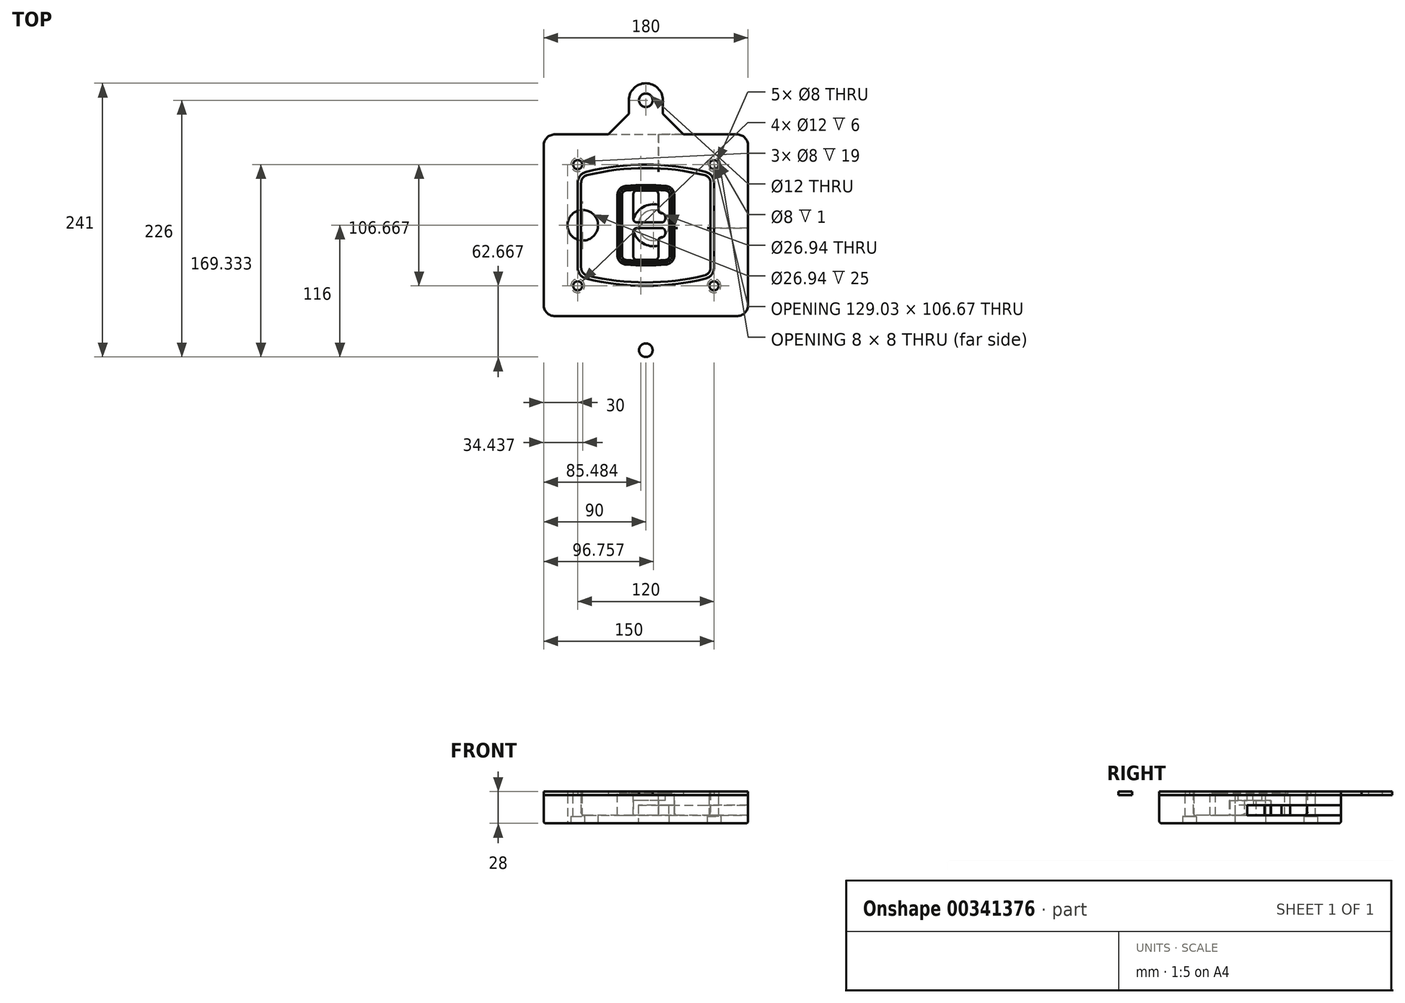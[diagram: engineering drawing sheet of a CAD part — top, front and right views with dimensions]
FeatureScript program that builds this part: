
annotation { "Feature Type Name" : "Feature", "Feature Type Description" : "" }
export const myFeature = defineFeature(function(context is Context, id is Id, definition is map)
    precondition{}
    {
        {
            var Q0;
            Q0=qCreatedBy(makeId("Top.planeOp"),FACE);
            var sketch = newSketch(context, id + "F0", { "sketchPlane" : qUnion([Q0])});
            skPoint(sketch, "E0.rect.middle", {"position": v(0, 0) * mm});
            skLineSegment(sketch, "E1.bottom", {"start": v(-80, -80) * mm, "end": v(80, -80) * mm});
            skLineSegment(sketch, "E1.top", {"start": v(-80, 80) * mm, "end": v(80, 80) * mm});
            skLineSegment(sketch, "E1.left", {"start": v(-90, -70) * mm, "end": v(-90, 70) * mm});
            skLineSegment(sketch, "E1.right", {"start": v(90, -70) * mm, "end": v(90, 70) * mm});
            skLineSegment(sketch, "E2", {"start": v(-90, 80) * mm, "end": v(90, -80) * mm, "construction": true});
            skLineSegment(sketch, "E3", {"start": v(90, 80) * mm, "end": v(-90, -80) * mm, "construction": true});
            skCircle(sketch, "E4", {"center": v(-60, 53.33) * mm, "radius": 4 * mm});
            skCircle(sketch, "E5", {"center": v(60, 53.33) * mm, "radius": 4 * mm});
            skCircle(sketch, "E6", {"center": v(60, -53.33) * mm, "radius": 4 * mm});
            skCircle(sketch, "E7", {"center": v(-60, -53.33) * mm, "radius": 4 * mm});
            skLineSegment(sketch, "E8", {"start": v(-60, 53.33) * mm, "end": v(60, 53.33) * mm, "construction": true});
            skLineSegment(sketch, "E9", {"start": v(60, 53.33) * mm, "end": v(60, -53.33) * mm, "construction": true});
            skLineSegment(sketch, "E10", {"start": v(60, -53.33) * mm, "end": v(-60, -53.33) * mm, "construction": true});
            skLineSegment(sketch, "E11", {"start": v(-60, -53.33) * mm, "end": v(-60, 53.33) * mm, "construction": true});
            skLineSegment(sketch, "E12", {"start": v(-60, 37.3) * mm, "end": v(-60, -37.3) * mm});
            skLineSegment(sketch, "E13", {"start": v(60, 37.3) * mm, "end": v(60, -37.3) * mm});
            skArc(sketch, "E14", {"start": v(52.38, 47.01) * mm, "mid": v(0, 53.33) * mm, "end": v(-52.38, 47.01) * mm});
            skArc(sketch, "E15", {"start": v(-52.38, -47.01) * mm, "mid": v(0, -53.33) * mm, "end": v(52.38, -47.01) * mm});
            skLineSegment(sketch, "E16", {"start": v(-60, 0) * mm, "end": v(60, 0) * mm, "construction": true});
            skPoint(sketch, "E17.visualSharp", {"position": v(-60, -45) * mm});
            skArc(sketch, "E17.filletArc", {"start": v(-60, -37.3) * mm, "mid": v(-57.87, -43.47) * mm, "end": v(-52.38, -47.01) * mm});
            skPoint(sketch, "E18.visualSharp", {"position": v(-60, 45) * mm});
            skArc(sketch, "E18.filletArc", {"start": v(-52.38, 47.01) * mm, "mid": v(-57.87, 43.47) * mm, "end": v(-60, 37.3) * mm});
            skPoint(sketch, "E19.visualSharp", {"position": v(60, 45) * mm});
            skArc(sketch, "E19.filletArc", {"start": v(60, 37.3) * mm, "mid": v(57.87, 43.47) * mm, "end": v(52.38, 47.01) * mm});
            skPoint(sketch, "E20.visualSharp", {"position": v(60, -45) * mm});
            skArc(sketch, "E20.filletArc", {"start": v(52.38, -47.01) * mm, "mid": v(57.87, -43.47) * mm, "end": v(60, -37.3) * mm});
            skPoint(sketch, "E21.visualSharp", {"position": v(-90, 80) * mm});
            skArc(sketch, "E21.filletArc", {"start": v(-80, 80) * mm, "mid": v(-87.07, 77.07) * mm, "end": v(-90, 70) * mm});
            skPoint(sketch, "E22.visualSharp", {"position": v(90, 80) * mm});
            skArc(sketch, "E22.filletArc", {"start": v(90, 70) * mm, "mid": v(87.07, 77.07) * mm, "end": v(80, 80) * mm});
            skPoint(sketch, "E23.visualSharp", {"position": v(90, -80) * mm});
            skArc(sketch, "E23.filletArc", {"start": v(80, -80) * mm, "mid": v(87.07, -77.07) * mm, "end": v(90, -70) * mm});
            skPoint(sketch, "E24.visualSharp", {"position": v(-90, -80) * mm});
            skArc(sketch, "E24.filletArc", {"start": v(-90, -70) * mm, "mid": v(-87.07, -77.07) * mm, "end": v(-80, -80) * mm});
            skArc(sketch, "E25.0", {"start": v(57, 37.3) * mm, "mid": v(55.5, 41.62) * mm, "end": v(51.67, 44.1) * mm});
            skLineSegment(sketch, "E25.1", {"start": v(57, 37.3) * mm, "end": v(57, -37.3) * mm});
            skArc(sketch, "E25.2", {"start": v(51.67, -44.1) * mm, "mid": v(55.5, -41.62) * mm, "end": v(57, -37.3) * mm});
            skArc(sketch, "E25.3", {"start": v(-51.67, -44.1) * mm, "mid": v(0, -50.33) * mm, "end": v(51.67, -44.1) * mm});
            skArc(sketch, "E25.4", {"start": v(-57, -37.3) * mm, "mid": v(-55.5, -41.62) * mm, "end": v(-51.67, -44.1) * mm});
            skArc(sketch, "E25.5", {"start": v(51.67, 44.1) * mm, "mid": v(0, 50.33) * mm, "end": v(-51.67, 44.1) * mm});
            skLineSegment(sketch, "E25.6", {"start": v(-57, 37.3) * mm, "end": v(-57, -37.3) * mm});
            skArc(sketch, "E25.7", {"start": v(-51.67, 44.1) * mm, "mid": v(-55.5, 41.62) * mm, "end": v(-57, 37.3) * mm});
            skArc(sketch, "E26.0", {"start": v(-53.33, 50.9) * mm, "mid": v(-61.01, 45.94) * mm, "end": v(-64, 37.3) * mm});
            skArc(sketch, "E26.1", {"start": v(53.33, 50.9) * mm, "mid": v(0, 57.33) * mm, "end": v(-53.33, 50.9) * mm});
            skArc(sketch, "E26.2", {"start": v(64, 37.3) * mm, "mid": v(61.01, 45.94) * mm, "end": v(53.33, 50.9) * mm});
            skLineSegment(sketch, "E26.3", {"start": v(64, 37.3) * mm, "end": v(64, -37.3) * mm});
            skArc(sketch, "E26.4", {"start": v(53.33, -50.9) * mm, "mid": v(61.01, -45.94) * mm, "end": v(64, -37.3) * mm});
            skLineSegment(sketch, "E26.5", {"start": v(-64, 37.3) * mm, "end": v(-64, -37.3) * mm});
            skArc(sketch, "E26.6", {"start": v(-53.33, -50.9) * mm, "mid": v(0, -57.33) * mm, "end": v(53.33, -50.9) * mm});
            skArc(sketch, "E26.7", {"start": v(-64, -37.3) * mm, "mid": v(-61.01, -45.94) * mm, "end": v(-53.33, -50.9) * mm});
            skSolve(sketch);
        }
        {
            var Q0;
            Q0=makeQuery(id+"F0.imprint","IMPRINT",FACE,{"disambiguationData":[TD([[makeQuery(id+"F0.imprint","IMPRINT",EDGE,{"derivedFrom":sQuery(id+"F0.wireOp",EDGE,"E1.bottom")}),1.0]])]});
            var Q1;
            Q1=makeQuery(id+"F0.imprint","IMPRINT",FACE,{"disambiguationData":[TD([[makeQuery(id+"F0.imprint","IMPRINT",EDGE,{"derivedFrom":sQuery(id+"F0.wireOp",EDGE,"E12")}),1.0]])]});
            var Q2;
            Q2=makeQuery(id+"F0.imprint","IMPRINT",FACE,{"disambiguationData":[TD([[makeQuery(id+"F0.imprint","IMPRINT",EDGE,{"derivedFrom":sQuery(id+"F0.wireOp",EDGE,"E25.0")}),1.0]])]});
            var Q3;
            Q3=makeQuery(id+"F0.imprint","IMPRINT",FACE,{"disambiguationData":[TD([[makeQuery(id+"F0.imprint","IMPRINT",EDGE,{"derivedFrom":sQuery(id+"F0.wireOp",EDGE,"E12")}),-1.0]])]});
            extrude(context, id + "F1", {"entities" : qUnion([Q0, Q1, Q2, Q3]), "oppositeDirection" : true, "depth" : 25 * mm});
        }
        {
            var Q0;
            Q0=makeQuery(id+"F0.imprint","IMPRINT",FACE,{"disambiguationData":[TD([[makeQuery(id+"F0.imprint","IMPRINT",EDGE,{"derivedFrom":sQuery(id+"F0.wireOp",EDGE,"E12")}),1.0]])]});
            extrude(context, id + "F2", {"entities" : qUnion([Q0]), "operationType" : NewBodyOperationType.ADD, "depth" : 3 * mm});
        }
        {
            var Q0;
            Q0=makeQuery(id+"F0.imprint","IMPRINT",FACE,{"disambiguationData":[TD([[makeQuery(id+"F0.imprint","IMPRINT",EDGE,{"derivedFrom":sQuery(id+"F0.wireOp",EDGE,"E25.0")}),1.0]])]});
            extrude(context, id + "F3", {"entities" : qUnion([Q0]), "operationType" : NewBodyOperationType.REMOVE, "oppositeDirection" : true, "depth" : 18 * mm});
        }
        {
            var Q0;
            Q0=makeQuery(id+"F2.opExtrude","CAP_FACE",FACE,{"disambiguationData":[OSD([sQuery(id+"F0.wireOp",EDGE,"E12"),sQuery(id+"F0.wireOp",EDGE,"E13"),sQuery(id+"F0.wireOp",EDGE,"E14"),sQuery(id+"F0.wireOp",EDGE,"E15"),sQuery(id+"F0.wireOp",EDGE,"E17.filletArc"),sQuery(id+"F0.wireOp",EDGE,"E18.filletArc"),sQuery(id+"F0.wireOp",EDGE,"E19.filletArc"),sQuery(id+"F0.wireOp",EDGE,"E20.filletArc"),sQuery(id+"F0.wireOp",EDGE,"E25.0"),sQuery(id+"F0.wireOp",EDGE,"E25.1"),sQuery(id+"F0.wireOp",EDGE,"E25.2"),sQuery(id+"F0.wireOp",EDGE,"E25.3"),sQuery(id+"F0.wireOp",EDGE,"E25.4"),sQuery(id+"F0.wireOp",EDGE,"E25.5"),sQuery(id+"F0.wireOp",EDGE,"E25.6"),sQuery(id+"F0.wireOp",EDGE,"E25.7")])],"isStart":false});
            var sketch = newSketch(context, id + "F4", { "sketchPlane" : qUnion([Q0])});
            skArc(sketch, "E27.0", {"start": v(-17.7, -34.56) * mm, "mid": v(0, -35.33) * mm, "end": v(17.7, -34.56) * mm});
            skArc(sketch, "E28.0", {"start": v(17.7, 34.56) * mm, "mid": v(0, 35.33) * mm, "end": v(-17.7, 34.56) * mm});
            skLineSegment(sketch, "E29", {"start": v(-25, 26.59) * mm, "end": v(-25, -26.59) * mm});
            skLineSegment(sketch, "E30", {"start": v(25, 26.59) * mm, "end": v(25, -26.59) * mm});
            skLineSegment(sketch, "E31", {"start": v(-25, 33.78) * mm, "end": v(25, 33.78) * mm, "construction": true});
            skLineSegment(sketch, "E32", {"start": v(-25, -33.78) * mm, "end": v(25, -33.78) * mm, "construction": true});
            skPoint(sketch, "E33.visualSharp", {"position": v(-25, 33.78) * mm});
            skArc(sketch, "E33.filletArc", {"start": v(-17.7, 34.56) * mm, "mid": v(-22.9, 32) * mm, "end": v(-25, 26.59) * mm});
            skPoint(sketch, "E34.visualSharp", {"position": v(25, 33.78) * mm});
            skArc(sketch, "E34.filletArc", {"start": v(25, 26.59) * mm, "mid": v(22.9, 32) * mm, "end": v(17.7, 34.56) * mm});
            skPoint(sketch, "E35.visualSharp", {"position": v(25, -33.78) * mm});
            skArc(sketch, "E35.filletArc", {"start": v(17.7, -34.56) * mm, "mid": v(22.9, -32) * mm, "end": v(25, -26.59) * mm});
            skPoint(sketch, "E36.visualSharp", {"position": v(-25, -33.78) * mm});
            skArc(sketch, "E36.filletArc", {"start": v(-25, -26.59) * mm, "mid": v(-22.9, -32) * mm, "end": v(-17.7, -34.56) * mm});
            skArc(sketch, "E37.0", {"start": v(51.67, 44.1) * mm, "mid": v(0, 50.33) * mm, "end": v(-51.67, 44.1) * mm});
            skArc(sketch, "E37.1", {"start": v(-51.67, 44.1) * mm, "mid": v(-55.5, 41.62) * mm, "end": v(-57, 37.3) * mm});
            skLineSegment(sketch, "E37.2", {"start": v(-57, 37.3) * mm, "end": v(-57, -37.3) * mm});
            skArc(sketch, "E37.3", {"start": v(-57, -37.3) * mm, "mid": v(-55.5, -41.62) * mm, "end": v(-51.67, -44.1) * mm});
            skArc(sketch, "E37.4", {"start": v(-51.67, -44.1) * mm, "mid": v(0, -50.33) * mm, "end": v(51.67, -44.1) * mm});
            skArc(sketch, "E37.5", {"start": v(51.67, -44.1) * mm, "mid": v(55.5, -41.62) * mm, "end": v(57, -37.3) * mm});
            skLineSegment(sketch, "E37.6", {"start": v(57, 37.3) * mm, "end": v(57, -37.3) * mm});
            skArc(sketch, "E37.7", {"start": v(57, 37.3) * mm, "mid": v(55.5, 41.62) * mm, "end": v(51.67, 44.1) * mm});
            skLineSegment(sketch, "E38.0", {"start": v(23, 26.59) * mm, "end": v(23, -26.59) * mm});
            skArc(sketch, "E38.1", {"start": v(17.53, -32.56) * mm, "mid": v(21.42, -30.64) * mm, "end": v(23, -26.59) * mm});
            skArc(sketch, "E38.2", {"start": v(-17.53, -32.56) * mm, "mid": v(0, -33.33) * mm, "end": v(17.53, -32.56) * mm});
            skArc(sketch, "E38.3", {"start": v(-23, -26.59) * mm, "mid": v(-21.42, -30.64) * mm, "end": v(-17.53, -32.56) * mm});
            skLineSegment(sketch, "E38.4", {"start": v(-23, 26.59) * mm, "end": v(-23, -26.59) * mm});
            skArc(sketch, "E38.5", {"start": v(23, 26.59) * mm, "mid": v(21.42, 30.64) * mm, "end": v(17.53, 32.56) * mm});
            skArc(sketch, "E38.6", {"start": v(-17.53, 32.56) * mm, "mid": v(-21.42, 30.64) * mm, "end": v(-23, 26.59) * mm});
            skArc(sketch, "E38.7", {"start": v(17.53, 32.56) * mm, "mid": v(0, 33.33) * mm, "end": v(-17.53, 32.56) * mm});
            skArc(sketch, "E39.0", {"start": v(21, 26.59) * mm, "mid": v(19.95, 29.29) * mm, "end": v(17.35, 30.57) * mm});
            skLineSegment(sketch, "E39.1", {"start": v(21, 26.59) * mm, "end": v(21, -26.59) * mm});
            skArc(sketch, "E39.2", {"start": v(17.35, -30.57) * mm, "mid": v(19.95, -29.29) * mm, "end": v(21, -26.59) * mm});
            skArc(sketch, "E39.3", {"start": v(-17.35, -30.57) * mm, "mid": v(0, -31.33) * mm, "end": v(17.35, -30.57) * mm});
            skArc(sketch, "E39.4", {"start": v(-21, -26.59) * mm, "mid": v(-19.95, -29.29) * mm, "end": v(-17.35, -30.57) * mm});
            skArc(sketch, "E39.5", {"start": v(17.35, 30.57) * mm, "mid": v(0, 31.33) * mm, "end": v(-17.35, 30.57) * mm});
            skLineSegment(sketch, "E39.6", {"start": v(-21, 26.59) * mm, "end": v(-21, -26.59) * mm});
            skArc(sketch, "E39.7", {"start": v(-17.35, 30.57) * mm, "mid": v(-19.95, 29.29) * mm, "end": v(-21, 26.59) * mm});
            skLineSegment(sketch, "E40", {"start": v(-25, 0) * mm, "end": v(25, 0) * mm, "construction": true});
            skLineSegment(sketch, "E41", {"start": v(-11, 5.5) * mm, "end": v(-11, 27.5) * mm});
            skLineSegment(sketch, "E42", {"start": v(-8, 30.5) * mm, "end": v(8, 30.5) * mm});
            skLineSegment(sketch, "E43", {"start": v(11, 27.5) * mm, "end": v(11, 13.5) * mm});
            skLineSegment(sketch, "E44", {"start": v(14, 10.5) * mm, "end": v(14, 10.5) * mm});
            skLineSegment(sketch, "E45", {"start": v(17, 7.5) * mm, "end": v(17, 5.5) * mm});
            skLineSegment(sketch, "E46", {"start": v(14, 2.5) * mm, "end": v(-8, 2.5) * mm});
            skPoint(sketch, "E47.visualSharp", {"position": v(-11, 30.5) * mm});
            skArc(sketch, "E47.filletArc", {"start": v(-8, 30.5) * mm, "mid": v(-10.12, 29.62) * mm, "end": v(-11, 27.5) * mm});
            skPoint(sketch, "E48.visualSharp", {"position": v(11, 30.5) * mm});
            skArc(sketch, "E48.filletArc", {"start": v(11, 27.5) * mm, "mid": v(10.12, 29.62) * mm, "end": v(8, 30.5) * mm});
            skPoint(sketch, "E49.visualSharp", {"position": v(11, 10.5) * mm});
            skArc(sketch, "E49.filletArc", {"start": v(11, 13.5) * mm, "mid": v(11.88, 11.38) * mm, "end": v(14, 10.5) * mm});
            skPoint(sketch, "E50.visualSharp", {"position": v(17, 10.5) * mm});
            skArc(sketch, "E50.filletArc", {"start": v(17, 7.5) * mm, "mid": v(16.12, 9.62) * mm, "end": v(14, 10.5) * mm});
            skPoint(sketch, "E51.visualSharp", {"position": v(17, 2.5) * mm});
            skArc(sketch, "E51.filletArc", {"start": v(14, 2.5) * mm, "mid": v(16.12, 3.38) * mm, "end": v(17, 5.5) * mm});
            skPoint(sketch, "E52.visualSharp", {"position": v(-11, 2.5) * mm});
            skArc(sketch, "E52.filletArc", {"start": v(-11, 5.5) * mm, "mid": v(-10.12, 3.38) * mm, "end": v(-8, 2.5) * mm});
            skLineSegment(sketch, "E53.0.MirrorCS", {"start": v(14, -2.5) * mm, "end": v(-8, -2.5) * mm});
            skArc(sketch, "E54.0.MirrorCS", {"start": v(-11, -5.5) * mm, "mid": v(-10.12, -3.38) * mm, "end": v(-8, -2.5) * mm});
            skLineSegment(sketch, "E55.0.MirrorCS", {"start": v(-11, -5.5) * mm, "end": v(-11, -27.5) * mm});
            skArc(sketch, "E56.0.MirrorCS", {"start": v(-8, -30.5) * mm, "mid": v(-10.12, -29.62) * mm, "end": v(-11, -27.5) * mm});
            skLineSegment(sketch, "E57.0.MirrorCS", {"start": v(-8, -30.5) * mm, "end": v(8, -30.5) * mm});
            skArc(sketch, "E58.0.MirrorCS", {"start": v(11, -27.5) * mm, "mid": v(10.12, -29.62) * mm, "end": v(8, -30.5) * mm});
            skLineSegment(sketch, "E59.0.MirrorCS", {"start": v(11, -27.5) * mm, "end": v(11, -13.5) * mm});
            skArc(sketch, "E60.0.MirrorCS", {"start": v(11, -13.5) * mm, "mid": v(11.88, -11.38) * mm, "end": v(14, -10.5) * mm});
            skArc(sketch, "E61.0.MirrorCS", {"start": v(17, -7.5) * mm, "mid": v(16.12, -9.62) * mm, "end": v(14, -10.5) * mm});
            skLineSegment(sketch, "E62.0.MirrorCS", {"start": v(17, -7.5) * mm, "end": v(17, -5.5) * mm});
            skArc(sketch, "E63.0.MirrorCS", {"start": v(14, -2.5) * mm, "mid": v(16.12, -3.38) * mm, "end": v(17, -5.5) * mm});
            skSolve(sketch);
        }
        {
            var Q0;
            Q0=makeQuery(id+"F4.imprint","IMPRINT",FACE,{"disambiguationData":[TD([[makeQuery(id+"F4.imprint","IMPRINT",EDGE,{"derivedFrom":sQuery(id+"F4.wireOp",EDGE,"E27.0")}),1.0]])]});
            var Q1;
            Q1=makeQuery(id+"F4.imprint","IMPRINT",FACE,{"disambiguationData":[TD([[makeQuery(id+"F4.imprint","IMPRINT",EDGE,{"derivedFrom":sQuery(id+"F4.wireOp",EDGE,"E38.0")}),-1.0]])]});
            var Q2;
            Q2=makeQuery(id+"F4.imprint","IMPRINT",FACE,{"disambiguationData":[TD([[makeQuery(id+"F4.imprint","IMPRINT",EDGE,{"derivedFrom":sQuery(id+"F4.wireOp",EDGE,"E39.0")}),1.0]])]});
            extrude(context, id + "F5", {"entities" : qUnion([Q0, Q1, Q2]), "operationType" : NewBodyOperationType.ADD, "endBound" : BoundingType.UP_TO_NEXT, "oppositeDirection" : true, "depth" : 25 * mm});
        }
        {
            var Q0;
            Q0=makeQuery(id+"F4.imprint","IMPRINT",FACE,{"disambiguationData":[TD([[makeQuery(id+"F4.imprint","IMPRINT",EDGE,{"derivedFrom":sQuery(id+"F4.wireOp",EDGE,"E38.0")}),-1.0]])]});
            extrude(context, id + "F6", {"entities" : qUnion([Q0]), "operationType" : NewBodyOperationType.REMOVE, "oppositeDirection" : true, "depth" : 2 * mm});
        }
        {
            var Q0;
            Q0=makeQuery(id+"F1.opExtrude","CAP_FACE",FACE,{"disambiguationData":[OSD([sQuery(id+"F0.wireOp",EDGE,"E1.bottom"),sQuery(id+"F0.wireOp",EDGE,"E1.top"),sQuery(id+"F0.wireOp",EDGE,"E1.left"),sQuery(id+"F0.wireOp",EDGE,"E1.right"),sQuery(id+"F0.wireOp",EDGE,"E4"),sQuery(id+"F0.wireOp",EDGE,"E5"),sQuery(id+"F0.wireOp",EDGE,"E6"),sQuery(id+"F0.wireOp",EDGE,"E7"),sQuery(id+"F0.wireOp",EDGE,"E21.filletArc"),sQuery(id+"F0.wireOp",EDGE,"E22.filletArc"),sQuery(id+"F0.wireOp",EDGE,"E23.filletArc"),sQuery(id+"F0.wireOp",EDGE,"E24.filletArc")])],"isStart":false});
            var sketch = newSketch(context, id + "F7", { "sketchPlane" : qUnion([Q0])});
            skCircle(sketch, "E64", {"center": v(6.76, 0) * mm, "radius": 13.47 * mm});
            skCircle(sketch, "E65", {"center": v(-55.56, 0) * mm, "radius": 13.47 * mm});
            skLineSegment(sketch, "E66", {"start": v(90, 0) * mm, "end": v(-90, 0) * mm});
            skCircle(sketch, "E67", {"center": v(6.76, 0) * mm, "radius": 18.47 * mm});
            skCircle(sketch, "E68", {"center": v(60, -53.33) * mm, "radius": 6 * mm});
            skCircle(sketch, "E69", {"center": v(-60, -53.33) * mm, "radius": 6 * mm});
            skCircle(sketch, "E70", {"center": v(-60, 53.33) * mm, "radius": 6 * mm});
            skCircle(sketch, "E71", {"center": v(60, 53.33) * mm, "radius": 6 * mm});
            skSolve(sketch);
        }
        {
            var Q0;
            {var subQ1=sQuery(id+"F7.wireOp",EDGE,"E66");var subQ4=sQuery(id+"F7.wireOp",EDGE,"E64");var subQ6=makeQuery(id+"F7.imprint","INTERSECT",VERTEX,{"disambiguationData":[OD(0.0)],"derivedFrom":[subQ4,subQ1]});Q0=makeQuery(id+"F7.imprint","IMPRINT",FACE,{"disambiguationData":[TD([[makeQuery(id+"F7.imprint","IMPRINT",EDGE,{"disambiguationData":[TD([[subQ6,-1.0]])],"derivedFrom":subQ4}),-1.0]])]});}
            var Q1;
            {var subQ0=sQuery(id+"F7.wireOp",EDGE,"E66");var subQ1=sQuery(id+"F7.wireOp",EDGE,"E64");var subQ3=makeQuery(id+"F7.imprint","INTERSECT",VERTEX,{"disambiguationData":[OD(0.0)],"derivedFrom":[subQ1,subQ0]});Q1=makeQuery(id+"F7.imprint","IMPRINT",FACE,{"disambiguationData":[TD([[makeQuery(id+"F7.imprint","IMPRINT",EDGE,{"disambiguationData":[TD([[subQ3,-1.0]])],"derivedFrom":subQ1}),1.0]])]});}
            var Q2;
            {var subQ0=sQuery(id+"F7.wireOp",EDGE,"E66");var subQ1=sQuery(id+"F7.wireOp",EDGE,"E64");var subQ3=makeQuery(id+"F7.imprint","INTERSECT",VERTEX,{"disambiguationData":[OD(0.0)],"derivedFrom":[subQ1,subQ0]});Q2=makeQuery(id+"F7.imprint","IMPRINT",FACE,{"disambiguationData":[TD([[makeQuery(id+"F7.imprint","IMPRINT",EDGE,{"disambiguationData":[TD([[subQ3,1.0]])],"derivedFrom":subQ1}),1.0]])]});}
            var Q3;
            {var subQ1=sQuery(id+"F7.wireOp",EDGE,"E66");var subQ4=sQuery(id+"F7.wireOp",EDGE,"E64");var subQ6=makeQuery(id+"F7.imprint","INTERSECT",VERTEX,{"disambiguationData":[OD(0.0)],"derivedFrom":[subQ4,subQ1]});Q3=makeQuery(id+"F7.imprint","IMPRINT",FACE,{"disambiguationData":[TD([[makeQuery(id+"F7.imprint","IMPRINT",EDGE,{"disambiguationData":[TD([[subQ6,1.0]])],"derivedFrom":subQ4}),-1.0]])]});}
            extrude(context, id + "F8", {"entities" : qUnion([Q0, Q1, Q2, Q3]), "operationType" : NewBodyOperationType.ADD, "oppositeDirection" : true, "depth" : 20 * mm});
        }
        {
            var Q0;
            {var subQ0=sQuery(id+"F7.wireOp",EDGE,"E66");var subQ1=sQuery(id+"F7.wireOp",EDGE,"E64");var subQ3=makeQuery(id+"F7.imprint","INTERSECT",VERTEX,{"disambiguationData":[OD(0.0)],"derivedFrom":[subQ1,subQ0]});Q0=makeQuery(id+"F7.imprint","IMPRINT",FACE,{"disambiguationData":[TD([[makeQuery(id+"F7.imprint","IMPRINT",EDGE,{"disambiguationData":[TD([[subQ3,-1.0]])],"derivedFrom":subQ1}),1.0]])]});}
            var Q1;
            {var subQ0=sQuery(id+"F7.wireOp",EDGE,"E66");var subQ1=sQuery(id+"F7.wireOp",EDGE,"E64");var subQ3=makeQuery(id+"F7.imprint","INTERSECT",VERTEX,{"disambiguationData":[OD(0.0)],"derivedFrom":[subQ1,subQ0]});Q1=makeQuery(id+"F7.imprint","IMPRINT",FACE,{"disambiguationData":[TD([[makeQuery(id+"F7.imprint","IMPRINT",EDGE,{"disambiguationData":[TD([[subQ3,1.0]])],"derivedFrom":subQ1}),1.0]])]});}
            extrude(context, id + "F9", {"entities" : qUnion([Q0, Q1]), "operationType" : NewBodyOperationType.REMOVE, "oppositeDirection" : true, "depth" : 16 * mm});
        }
        {
            var Q0;
            {var subQ0=sQuery(id+"F7.wireOp",EDGE,"E66");var subQ1=sQuery(id+"F7.wireOp",EDGE,"E65");var subQ3=makeQuery(id+"F7.imprint","INTERSECT",VERTEX,{"disambiguationData":[OD(0.0)],"derivedFrom":[subQ1,subQ0]});Q0=makeQuery(id+"F7.imprint","IMPRINT",FACE,{"disambiguationData":[TD([[makeQuery(id+"F7.imprint","IMPRINT",EDGE,{"disambiguationData":[TD([[subQ3,-1.0]])],"derivedFrom":subQ1}),1.0]])]});}
            var Q1;
            {var subQ0=sQuery(id+"F7.wireOp",EDGE,"E66");var subQ1=sQuery(id+"F7.wireOp",EDGE,"E65");var subQ3=makeQuery(id+"F7.imprint","INTERSECT",VERTEX,{"disambiguationData":[OD(0.0)],"derivedFrom":[subQ1,subQ0]});Q1=makeQuery(id+"F7.imprint","IMPRINT",FACE,{"disambiguationData":[TD([[makeQuery(id+"F7.imprint","IMPRINT",EDGE,{"disambiguationData":[TD([[subQ3,1.0]])],"derivedFrom":subQ1}),1.0]])]});}
            extrude(context, id + "F10", {"entities" : qUnion([Q0, Q1]), "operationType" : NewBodyOperationType.REMOVE, "oppositeDirection" : true, "depth" : 25 * mm});
        }
        {
            var Q0;
            Q0=makeQuery(id+"F7.imprint","IMPRINT",FACE,{"disambiguationData":[TD([[makeQuery(id+"F7.imprint","IMPRINT",EDGE,{"derivedFrom":sQuery(id+"F7.wireOp",EDGE,"E68")}),1.0]])]});
            var Q1;
            Q1=makeQuery(id+"F7.imprint","IMPRINT",FACE,{"disambiguationData":[TD([[makeQuery(id+"F7.imprint","IMPRINT",EDGE,{"derivedFrom":makeQuery(id+"F1.opExtrude","CAP_EDGE",EDGE,{"disambiguationData":[OSD([sQuery(id+"F0.wireOp",EDGE,"E5")])],"isStart":false})}),-1.0]])]});
            var Q2;
            Q2=makeQuery(id+"F7.imprint","IMPRINT",FACE,{"disambiguationData":[TD([[makeQuery(id+"F7.imprint","IMPRINT",EDGE,{"derivedFrom":sQuery(id+"F7.wireOp",EDGE,"E69")}),1.0]])]});
            var Q3;
            Q3=makeQuery(id+"F7.imprint","IMPRINT",FACE,{"disambiguationData":[TD([[makeQuery(id+"F7.imprint","IMPRINT",EDGE,{"derivedFrom":makeQuery(id+"F1.opExtrude","CAP_EDGE",EDGE,{"disambiguationData":[OSD([sQuery(id+"F0.wireOp",EDGE,"E4")])],"isStart":false})}),-1.0]])]});
            var Q4;
            Q4=makeQuery(id+"F7.imprint","IMPRINT",FACE,{"disambiguationData":[TD([[makeQuery(id+"F7.imprint","IMPRINT",EDGE,{"derivedFrom":sQuery(id+"F7.wireOp",EDGE,"E70")}),1.0]])]});
            var Q5;
            Q5=makeQuery(id+"F7.imprint","IMPRINT",FACE,{"disambiguationData":[TD([[makeQuery(id+"F7.imprint","IMPRINT",EDGE,{"derivedFrom":makeQuery(id+"F1.opExtrude","CAP_EDGE",EDGE,{"disambiguationData":[OSD([sQuery(id+"F0.wireOp",EDGE,"E7")])],"isStart":false})}),-1.0]])]});
            var Q6;
            Q6=makeQuery(id+"F7.imprint","IMPRINT",FACE,{"disambiguationData":[TD([[makeQuery(id+"F7.imprint","IMPRINT",EDGE,{"derivedFrom":sQuery(id+"F7.wireOp",EDGE,"E71")}),1.0]])]});
            var Q7;
            Q7=makeQuery(id+"F7.imprint","IMPRINT",FACE,{"disambiguationData":[TD([[makeQuery(id+"F7.imprint","IMPRINT",EDGE,{"derivedFrom":makeQuery(id+"F1.opExtrude","CAP_EDGE",EDGE,{"disambiguationData":[OSD([sQuery(id+"F0.wireOp",EDGE,"E6")])],"isStart":false})}),-1.0]])]});
            extrude(context, id + "F11", {"entities" : qUnion([Q0, Q1, Q2, Q3, Q4, Q5, Q6, Q7]), "operationType" : NewBodyOperationType.REMOVE, "oppositeDirection" : true, "depth" : 6 * mm});
        }
        {
            var Q0;
            Q0=makeQuery(id+"F9.boolean.opBoolean","COPY",FACE,{"derivedFrom":makeQuery(id+"F9.opExtrude","CAP_FACE",FACE,{"disambiguationData":[OSD([sQuery(id+"F7.wireOp",EDGE,"E64")])],"isStart":false})});
            var sketch = newSketch(context, id + "F12", { "sketchPlane" : qUnion([Q0])});
            skArc(sketch, "E72.0", {"start": v(11, -88.19) * mm, "mid": v(97.1, -83.6) * mm, "end": v(92.5, 2.5) * mm});
            skLineSegment(sketch, "E72.1", {"start": v(11, -17.97) * mm, "end": v(11, -17.97) * mm});
            skLineSegment(sketch, "E73", {"start": v(92.5, -105.13) * mm, "end": v(102.3, -105.13) * mm});
            skLineSegment(sketch, "E74.0", {"start": v(92.5, 2.5) * mm, "end": v(14, 2.5) * mm});
            skArc(sketch, "E74.1", {"start": v(14, 2.5) * mm, "mid": v(16.12, 3.38) * mm, "end": v(17, 5.5) * mm});
            skLineSegment(sketch, "E74.2", {"start": v(17, 7.5) * mm, "end": v(17, 5.5) * mm});
            skArc(sketch, "E74.3", {"start": v(17, 7.5) * mm, "mid": v(16.12, 9.62) * mm, "end": v(14, 10.5) * mm});
            skArc(sketch, "E74.4", {"start": v(11, 13.5) * mm, "mid": v(11.88, 11.38) * mm, "end": v(14, 10.5) * mm});
            skLineSegment(sketch, "E74.5", {"start": v(11, 13.5) * mm, "end": v(11, -88.19) * mm});
            skLineSegment(sketch, "E74.7", {"start": v(92.5, -2.5) * mm, "end": v(14, -2.5) * mm});
            skArc(sketch, "E74.8", {"start": v(14, -2.5) * mm, "mid": v(16.12, -3.38) * mm, "end": v(17, -5.5) * mm});
            skLineSegment(sketch, "E74.9", {"start": v(17, -7.5) * mm, "end": v(17, -5.5) * mm});
            skArc(sketch, "E74.10", {"start": v(17, -7.5) * mm, "mid": v(16.12, -9.62) * mm, "end": v(14, -10.5) * mm});
            skArc(sketch, "E74.11", {"start": v(11, -13.5) * mm, "mid": v(11.88, -11.38) * mm, "end": v(14, -10.5) * mm});
            skLineSegment(sketch, "E74.12", {"start": v(11, -17.97) * mm, "end": v(11, -13.5) * mm});
            skPoint(sketch, "E75.orphan", {"position": v(11, -27.5) * mm});
            skPoint(sketch, "E76.orphan", {"position": v(-8, -2.5) * mm});
            skPoint(sketch, "E77.orphan", {"position": v(-8, 2.5) * mm});
            skPoint(sketch, "E78.orphan", {"position": v(11, 27.5) * mm});
            skSolve(sketch);
        }
        {
            var Q0;
            {var subQ7=sQuery(id+"F12.wireOp",EDGE,"E72.0");var subQ14=sQuery(id+"F12.wireOp",EDGE,"E72.1");var subQ16=sQuery(id+"F12.wireOp",EDGE,"E74.1");var subQ18=sQuery(id+"F12.wireOp",EDGE,"E74.8");Q0=qUnion([makeQuery(id+"F12.imprint","IMPRINT",FACE,{"disambiguationData":[TD([[makeQuery(id+"F12.imprint","IMPRINT",EDGE,{"derivedFrom":subQ7}),1.0]])]}),makeQuery(id+"F12.imprint","IMPRINT",FACE,{"disambiguationData":[TD([[makeQuery(id+"F12.imprint","IMPRINT",EDGE,{"derivedFrom":subQ14}),1.0]])]}),makeQuery(id+"F12.imprint","IMPRINT",FACE,{"disambiguationData":[TD([[makeQuery(id+"F12.imprint","IMPRINT",EDGE,{"derivedFrom":subQ16}),1.0]])]}),makeQuery(id+"F12.imprint","IMPRINT",FACE,{"disambiguationData":[TD([[makeQuery(id+"F12.imprint","IMPRINT",EDGE,{"derivedFrom":subQ18}),-1.0]])]})]);}
            var Q1;
            Q1=makeQuery(id+"F5.boolean.opBoolean","SPLIT",FACE,{"disambiguationData":[TD([makeQuery(id+"F5.opExtrude","SWEPT_FACE",FACE,{"disambiguationData":[OSD([sQuery(id+"F4.wireOp",EDGE,"E41")])]})])],"derivedFrom":makeQuery(id+"F3.boolean.opBoolean","COPY",FACE,{"derivedFrom":makeQuery(id+"F3.opExtrude","CAP_FACE",FACE,{"disambiguationData":[OSD([sQuery(id+"F0.wireOp",EDGE,"E25.0"),sQuery(id+"F0.wireOp",EDGE,"E25.1"),sQuery(id+"F0.wireOp",EDGE,"E25.2"),sQuery(id+"F0.wireOp",EDGE,"E25.3"),sQuery(id+"F0.wireOp",EDGE,"E25.4"),sQuery(id+"F0.wireOp",EDGE,"E25.5"),sQuery(id+"F0.wireOp",EDGE,"E25.6"),sQuery(id+"F0.wireOp",EDGE,"E25.7")])],"isStart":false})})});
            extrude(context, id + "F13", {"entities" : qUnion([Q0]), "operationType" : NewBodyOperationType.REMOVE, "endBound" : BoundingType.UP_TO_SURFACE, "endBoundEntityFace" : qUnion([Q1]), "depth" : 25 * mm});
        }
        {
            var Q0;
            Q0=makeQuery(id+"F3.boolean.opBoolean","COPY",EDGE,{"derivedFrom":makeQuery(id+"F3.opExtrude","CAP_EDGE",EDGE,{"disambiguationData":[OSD([sQuery(id+"F0.wireOp",EDGE,"E25.6")])],"isStart":false})});
            var Q1;
            Q1=makeQuery(id+"F8.boolean.opBoolean","INTERSECT",EDGE,{"derivedFrom":[makeQuery(id+"F5.opExtrude","SWEPT_FACE",FACE,{"disambiguationData":[OSD([sQuery(id+"F4.wireOp",EDGE,"E30")])]}),makeQuery(id+"F8.opExtrude","CAP_FACE",FACE,{"disambiguationData":[OSD([sQuery(id+"F7.wireOp",EDGE,"E67")])],"isStart":false})]});
            var Q2;
            Q2=makeQuery(id+"F8.boolean.opBoolean","INTERSECT",EDGE,{"disambiguationData":[OD(1.0)],"derivedFrom":[makeQuery(id+"F5.opExtrude","SWEPT_FACE",FACE,{"disambiguationData":[OSD([sQuery(id+"F4.wireOp",EDGE,"E30")])]}),makeQuery(id+"F8.opExtrude","SWEPT_FACE",FACE,{"disambiguationData":[OSD([sQuery(id+"F7.wireOp",EDGE,"E67")])]})]});
            var Q3;
            {var subQ0=makeQuery(id+"F3.boolean.opBoolean","COPY",FACE,{"derivedFrom":makeQuery(id+"F3.opExtrude","CAP_FACE",FACE,{"disambiguationData":[OSD([sQuery(id+"F0.wireOp",EDGE,"E25.0"),sQuery(id+"F0.wireOp",EDGE,"E25.1"),sQuery(id+"F0.wireOp",EDGE,"E25.2"),sQuery(id+"F0.wireOp",EDGE,"E25.3"),sQuery(id+"F0.wireOp",EDGE,"E25.4"),sQuery(id+"F0.wireOp",EDGE,"E25.5"),sQuery(id+"F0.wireOp",EDGE,"E25.6"),sQuery(id+"F0.wireOp",EDGE,"E25.7")])],"isStart":false})});var subQ1=sQuery(id+"F4.wireOp",EDGE,"E30");Q3=makeQuery(id+"F8.boolean.opBoolean","SPLIT",EDGE,{"disambiguationData":[TD([makeQuery(id+"F5.opExtrude","SWEPT_FACE",FACE,{"disambiguationData":[OSD([sQuery(id+"F4.wireOp",EDGE,"E35.filletArc")])]})])],"derivedFrom":makeQuery(id+"F5.opExtrude","TWEAK_EDGE",EDGE,{"derivedFrom":[subQ0,makeQuery(id+"F4.imprint","IMPRINT",EDGE,{"derivedFrom":subQ1})]})});}
            var Q4;
            {var subQ0=sQuery(id+"F0.wireOp",EDGE,"E25.0");var subQ1=sQuery(id+"F0.wireOp",EDGE,"E25.1");var subQ2=sQuery(id+"F0.wireOp",EDGE,"E25.2");var subQ3=sQuery(id+"F0.wireOp",EDGE,"E25.3");var subQ4=sQuery(id+"F0.wireOp",EDGE,"E25.4");var subQ5=sQuery(id+"F0.wireOp",EDGE,"E25.5");var subQ6=sQuery(id+"F0.wireOp",EDGE,"E25.6");var subQ7=sQuery(id+"F0.wireOp",EDGE,"E25.7");Q4=makeQuery(id+"F8.boolean.opBoolean","INTERSECT",EDGE,{"derivedFrom":[makeQuery(id+"F5.boolean.opBoolean","SPLIT",FACE,{"disambiguationData":[TD([makeQuery(id+"F2.opExtrude","SWEPT_FACE",FACE,{"disambiguationData":[OSD([subQ0])]})])],"derivedFrom":makeQuery(id+"F3.boolean.opBoolean","COPY",FACE,{"derivedFrom":makeQuery(id+"F3.opExtrude","CAP_FACE",FACE,{"disambiguationData":[OSD([subQ0,subQ1,subQ2,subQ3,subQ4,subQ5,subQ6,subQ7])],"isStart":false})})}),makeQuery(id+"F8.opExtrude","SWEPT_FACE",FACE,{"disambiguationData":[OSD([sQuery(id+"F7.wireOp",EDGE,"E67")])]})]});}
            var Q5;
            Q5=makeQuery(id+"F8.boolean.opBoolean","INTERSECT",EDGE,{"disambiguationData":[OD(0.0)],"derivedFrom":[makeQuery(id+"F5.opExtrude","SWEPT_FACE",FACE,{"disambiguationData":[OSD([sQuery(id+"F4.wireOp",EDGE,"E30")])]}),makeQuery(id+"F8.opExtrude","SWEPT_FACE",FACE,{"disambiguationData":[OSD([sQuery(id+"F7.wireOp",EDGE,"E67")])]})]});
            fillet(context, id + "F14", {"entities" : qUnion([Q0, Q1, Q2, Q3, Q4, Q5]), "radius" : 3 * mm, "tangentPropagation" : true, "allowEdgeOverflow" : false});
        }
        {
            var Q0;
            Q0=makeQuery(id+"F1.opExtrude","CAP_EDGE",EDGE,{"disambiguationData":[OSD([sQuery(id+"F0.wireOp",EDGE,"E1.bottom")])],"isStart":false});
            fillet(context, id + "F15", {"entities" : qUnion([Q0]), "radius" : 2 * mm, "tangentPropagation" : true, "allowEdgeOverflow" : false});
        }
        {
            var Q0;
            {var subQ0=sQuery(id+"F0.wireOp",EDGE,"E21.filletArc");var subQ1=sQuery(id+"F0.wireOp",EDGE,"E7");var subQ2=sQuery(id+"F0.wireOp",EDGE,"E6");var subQ3=sQuery(id+"F0.wireOp",EDGE,"E5");var subQ4=sQuery(id+"F0.wireOp",EDGE,"E4");var subQ5=sQuery(id+"F0.wireOp",EDGE,"E22.filletArc");var subQ6=sQuery(id+"F0.wireOp",EDGE,"E1.bottom");var subQ7=sQuery(id+"F0.wireOp",EDGE,"E1.right");var subQ8=sQuery(id+"F0.wireOp",EDGE,"E1.top");var subQ9=sQuery(id+"F0.wireOp",EDGE,"E1.left");var subQ10=sQuery(id+"F0.wireOp",EDGE,"E23.filletArc");var subQ11=sQuery(id+"F0.wireOp",EDGE,"E24.filletArc");Q0=makeQuery(id+"F2.boolean.opBoolean","SPLIT",FACE,{"disambiguationData":[TD([makeQuery(id+"F1.opExtrude","SWEPT_FACE",FACE,{"disambiguationData":[OSD([subQ6])]})])],"derivedFrom":makeQuery(id+"F1.opExtrude","CAP_FACE",FACE,{"disambiguationData":[OSD([subQ6,subQ8,subQ9,subQ7,subQ4,subQ3,subQ2,subQ1,subQ0,subQ5,subQ10,subQ11])],"isStart":true})});}
            var sketch = newSketch(context, id + "F16", { "sketchPlane" : qUnion([Q0])});
            skArc(sketch, "E79", {"start": v(12.23, 118.68) * mm, "mid": v(-4.55, 124.3) * mm, "end": v(-15, 110) * mm});
            skCircle(sketch, "E80", {"center": v(0, 110) * mm, "radius": 0.06 * mm});
            skPoint(sketch, "E81.endSnap0", {"position": v(0, 80) * mm});
            skLineSegment(sketch, "E82", {"start": v(0, 110) * mm, "end": v(0, 80) * mm, "construction": true});
            skLineSegment(sketch, "E83", {"start": v(-15, 110) * mm, "end": v(-15, 98) * mm});
            skLineSegment(sketch, "E84", {"start": v(-15, 98) * mm, "end": v(-33, 80) * mm});
            skCircle(sketch, "E85", {"center": v(0, 110) * mm, "radius": 6 * mm});
            skLineSegment(sketch, "E86.MirrorCS", {"start": v(15, 110) * mm, "end": v(15, 98) * mm});
            skArc(sketch, "E87.MirrorCS", {"start": v(-12.23, 118.68) * mm, "mid": v(4.55, 124.3) * mm, "end": v(15, 110) * mm});
            skLineSegment(sketch, "E88.MirrorCS", {"start": v(15, 98) * mm, "end": v(33, 80) * mm});
            skPoint(sketch, "E89.endSnap0", {"position": v(60, 0) * mm});
            skLineSegment(sketch, "E90", {"start": v(-90, 0) * mm, "end": v(90, 0) * mm, "construction": true});
            skLineSegment(sketch, "E91.MirrorCS", {"start": v(0, -110) * mm, "end": v(0, -80) * mm, "construction": true});
            skCircle(sketch, "E92.MirrorC", {"center": v(0, -110) * mm, "radius": 6 * mm});
            skLineSegment(sketch, "E93.MirrorCS", {"start": v(-15, -110) * mm, "end": v(-15, -98) * mm});
            skArc(sketch, "E94.MirrorCS", {"start": v(12.23, -118.68) * mm, "mid": v(-4.55, -124.3) * mm, "end": v(-15, -110) * mm});
            skLineSegment(sketch, "E95.MirrorCS", {"start": v(15, -110) * mm, "end": v(15, -98) * mm});
            skLineSegment(sketch, "E96.MirrorCS", {"start": v(15, -98) * mm, "end": v(33, -80) * mm});
            skLineSegment(sketch, "E97.MirrorCS", {"start": v(-15, -98) * mm, "end": v(-33, -80) * mm});
            skArc(sketch, "E98.MirrorCS", {"start": v(-12.23, -118.68) * mm, "mid": v(4.55, -124.3) * mm, "end": v(15, -110) * mm});
            skSolve(sketch);
        }
        {
            var Q0;
            Q0=makeQuery(id+"F16.imprint","IMPRINT",FACE,{"disambiguationData":[TD([[makeQuery(id+"F16.imprint","IMPRINT",EDGE,{"derivedFrom":sQuery(id+"F16.wireOp",EDGE,"E85")}),-1.0]])]});
            var Q1;
            Q1=makeQuery(id+"F16.imprint","IMPRINT",FACE,{"disambiguationData":[TD([[makeQuery(id+"F16.imprint","IMPRINT",EDGE,{"derivedFrom":makeQuery(id+"F1.opExtrude","CAP_EDGE",EDGE,{"disambiguationData":[OSD([sQuery(id+"F0.wireOp",EDGE,"E1.left")])],"isStart":true})}),-1.0]])]});
            var Q2;
            Q2=makeQuery(id+"F16.imprint","IMPRINT",FACE,{"disambiguationData":[TD([[makeQuery(id+"F16.imprint","IMPRINT",EDGE,{"derivedFrom":sQuery(id+"F16.wireOp",EDGE,"E92.MirrorC")}),1.0]])]});
            var Q3;
            Q3=makeQuery(id+"F2.opExtrude","CAP_FACE",FACE,{"disambiguationData":[OSD([sQuery(id+"F0.wireOp",EDGE,"E12"),sQuery(id+"F0.wireOp",EDGE,"E13"),sQuery(id+"F0.wireOp",EDGE,"E14"),sQuery(id+"F0.wireOp",EDGE,"E15"),sQuery(id+"F0.wireOp",EDGE,"E17.filletArc"),sQuery(id+"F0.wireOp",EDGE,"E18.filletArc"),sQuery(id+"F0.wireOp",EDGE,"E19.filletArc"),sQuery(id+"F0.wireOp",EDGE,"E20.filletArc"),sQuery(id+"F0.wireOp",EDGE,"E25.0"),sQuery(id+"F0.wireOp",EDGE,"E25.1"),sQuery(id+"F0.wireOp",EDGE,"E25.2"),sQuery(id+"F0.wireOp",EDGE,"E25.3"),sQuery(id+"F0.wireOp",EDGE,"E25.4"),sQuery(id+"F0.wireOp",EDGE,"E25.5"),sQuery(id+"F0.wireOp",EDGE,"E25.6"),sQuery(id+"F0.wireOp",EDGE,"E25.7")])],"isStart":false});
            extrude(context, id + "F17", {"entities" : qUnion([Q0, Q1, Q2]), "endBound" : BoundingType.UP_TO_SURFACE, "endBoundEntityFace" : qUnion([Q3]), "depth" : 25 * mm});
        }
    });
